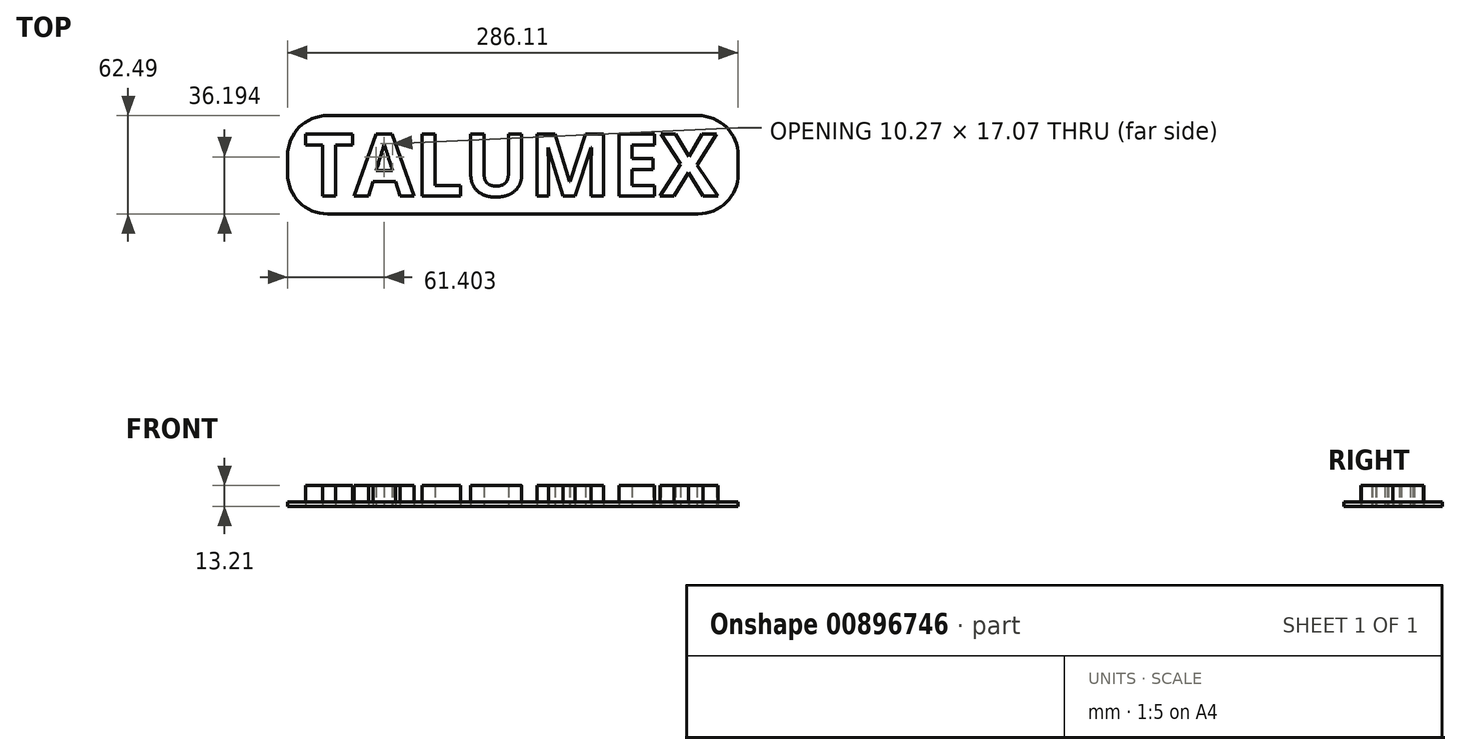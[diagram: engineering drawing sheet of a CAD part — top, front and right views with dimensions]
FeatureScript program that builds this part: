
annotation { "Feature Type Name" : "Feature", "Feature Type Description" : "" }
export const myFeature = defineFeature(function(context is Context, id is Id, definition is map)
    precondition{}
    {
        {
            var Q0;
            Q0=qCreatedBy(makeId("Top.planeOp"),FACE);
            var sketch = newSketch(context, id + "F0", { "sketchPlane" : qUnion([Q0])});
            skText(sketch, "E0", { "text": "TALUMEX", "fontName": "OpenSans-Bold.ttf"});
            const initialGuessF0  = {"E0": [-0.0737, -0.00757, 1, 0, 0.03977]};
            skSetInitialGuess(sketch, initialGuessF0);
            skSolve(sketch);
        }
        {
            var Q0;
            Q0 = qSketchRegion(id + "F0", true);
            extrude(context, id + "F1", {"entities" : qUnion([Q0]), "depth" : 13.2 * mm, "offsetDistance" : 25.4 * mm});
        }
        {
            var Q0;
            Q0=qCreatedBy(makeId("Top.planeOp"),FACE);
            var sketch = newSketch(context, id + "F2", { "sketchPlane" : qUnion([Q0])});
            skLineSegment(sketch, "E1.bottom", {"start": v(-84.01, -18.83) * mm, "end": v(202.1, -18.83) * mm});
            skLineSegment(sketch, "E1.top", {"start": v(-84.01, 43.66) * mm, "end": v(202.1, 43.66) * mm});
            skLineSegment(sketch, "E1.left", {"start": v(-84.01, -18.83) * mm, "end": v(-84.01, 43.66) * mm});
            skLineSegment(sketch, "E1.right", {"start": v(202.1, -18.83) * mm, "end": v(202.1, 43.66) * mm});
            skSolve(sketch);
        }
        {
            var Q0;
            Q0 = qSketchRegion(id + "F2", true);
            extrude(context, id + "F3", {"entities" : qUnion([Q0]), "depth" : 2.8 * mm, "offsetDistance" : 25.4 * mm});
        }
        {
            var Q0;
            Q0=makeQuery(id+"F3.opExtrude","SWEPT_EDGE",EDGE,{"disambiguationData":[OSD([sQuery(id+"F2.wireOp",EDGE,"E1.bottom"),sQuery(id+"F2.wireOp",EDGE,"E1.left")])]});
            var Q1;
            Q1=makeQuery(id+"F3.opExtrude","SWEPT_EDGE",EDGE,{"disambiguationData":[OSD([sQuery(id+"F2.wireOp",EDGE,"E1.top"),sQuery(id+"F2.wireOp",EDGE,"E1.left")])]});
            var Q2;
            Q2=makeQuery(id+"F3.opExtrude","SWEPT_EDGE",EDGE,{"disambiguationData":[OSD([sQuery(id+"F2.wireOp",EDGE,"E1.bottom"),sQuery(id+"F2.wireOp",EDGE,"E1.right")])]});
            var Q3;
            Q3=makeQuery(id+"F3.opExtrude","SWEPT_EDGE",EDGE,{"disambiguationData":[OSD([sQuery(id+"F2.wireOp",EDGE,"E1.top"),sQuery(id+"F2.wireOp",EDGE,"E1.right")])]});
            fillet(context, id + "F4", {"entities" : qUnion([Q0, Q1, Q2, Q3]), "radius" : 25.4 * mm, "tangentPropagation" : true, "allowEdgeOverflow" : false});
        }
    });
